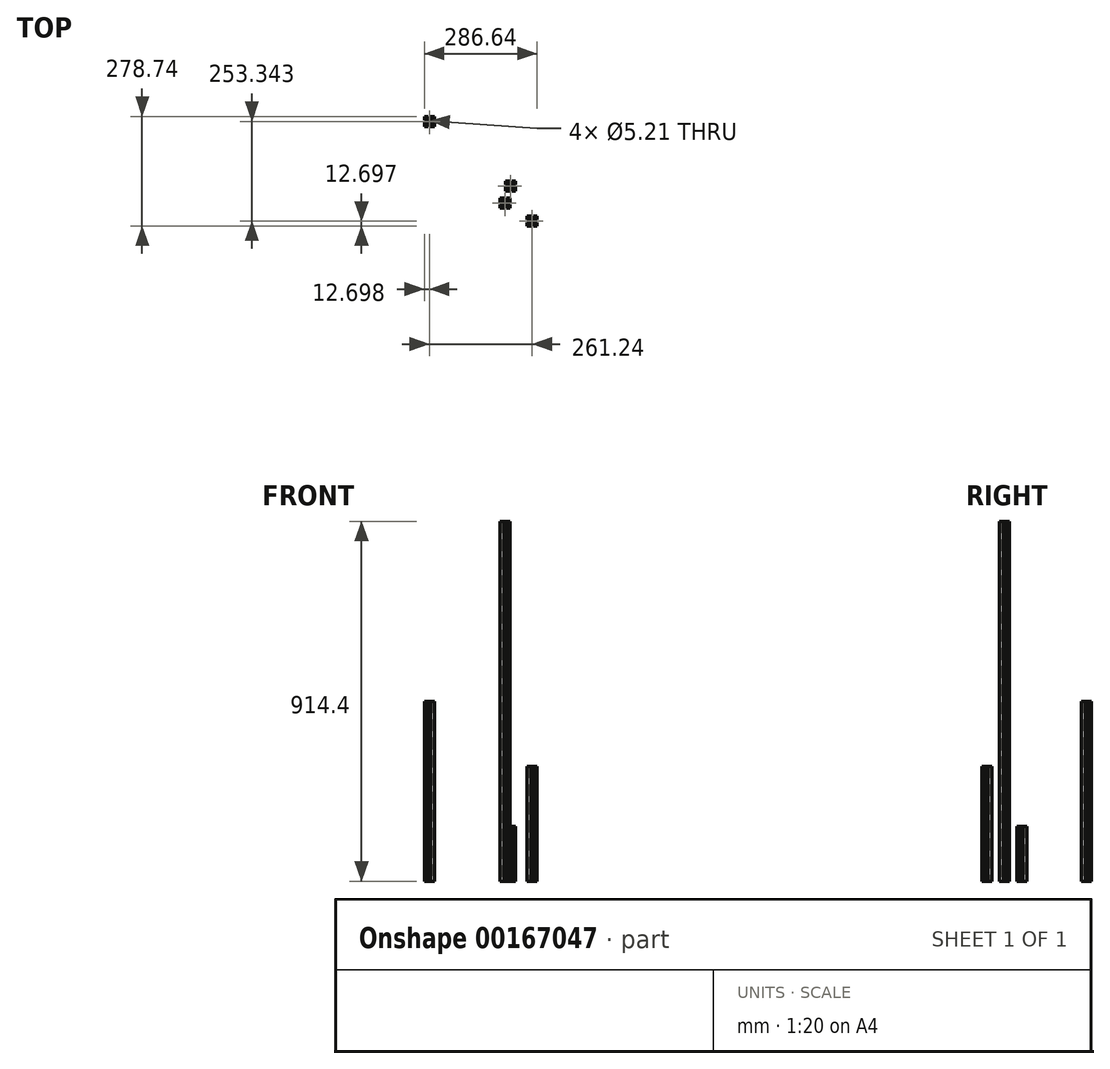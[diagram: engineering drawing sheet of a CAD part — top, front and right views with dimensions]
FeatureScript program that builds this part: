
annotation { "Feature Type Name" : "Feature", "Feature Type Description" : "" }
export const myFeature = defineFeature(function(context is Context, id is Id, definition is map)
    precondition{}
    {
        {
            var Q0;
            Q0=qCreatedBy(makeId("Top.planeOp"),FACE);
            var sketch = newSketch(context, id + "F0", { "sketchPlane" : qUnion([Q0])});
            skCircle(sketch, "E0", {"center": v(0, 0) * mm, "radius": 2.6 * mm});
            skLineSegment(sketch, "E1.bottom", {"start": v(-4.5, 4.5) * mm, "end": v(4.5, 4.5) * mm, "construction": true});
            skLineSegment(sketch, "E1.top", {"start": v(-4.5, -4.5) * mm, "end": v(4.5, -4.5) * mm, "construction": true});
            skLineSegment(sketch, "E1.left", {"start": v(-4.5, 4.5) * mm, "end": v(-4.5, -4.5) * mm, "construction": true});
            skLineSegment(sketch, "E1.right", {"start": v(4.5, 4.5) * mm, "end": v(4.5, -4.5) * mm, "construction": true});
            skPoint(sketch, "E2", {"position": v(-4.5, 0) * mm});
            skPoint(sketch, "E3", {"position": v(0, 4.5) * mm});
            skLineSegment(sketch, "E4", {"start": v(-2.54, 4.5) * mm, "end": v(2.54, 4.5) * mm});
            skLineSegment(sketch, "E5", {"start": v(2.54, 4.5) * mm, "end": v(8.2, 10.16) * mm});
            skLineSegment(sketch, "E6", {"start": v(8.2, 10.16) * mm, "end": v(3.24, 10.16) * mm});
            skLineSegment(sketch, "E7", {"start": v(3.24, 10.16) * mm, "end": v(3.24, 12.7) * mm});
            skLineSegment(sketch, "E8", {"start": v(3.24, 12.7) * mm, "end": v(12.7, 12.7) * mm});
            skLineSegment(sketch, "E9", {"start": v(12.7, 12.7) * mm, "end": v(12.7, 3.24) * mm});
            skLineSegment(sketch, "E10", {"start": v(12.7, 3.24) * mm, "end": v(10.16, 3.24) * mm});
            skLineSegment(sketch, "E11", {"start": v(10.16, 3.24) * mm, "end": v(10.16, 8.2) * mm});
            skLineSegment(sketch, "E12", {"start": v(10.16, 8.2) * mm, "end": v(4.5, 2.54) * mm});
            skLineSegment(sketch, "E13", {"start": v(4.5, 2.54) * mm, "end": v(4.5, -2.54) * mm});
            skLineSegment(sketch, "E14", {"start": v(4.5, -2.54) * mm, "end": v(10.16, -8.2) * mm});
            skLineSegment(sketch, "E15", {"start": v(10.16, -8.2) * mm, "end": v(10.16, -3.24) * mm});
            skLineSegment(sketch, "E16", {"start": v(10.16, -3.24) * mm, "end": v(12.7, -3.24) * mm});
            skLineSegment(sketch, "E17", {"start": v(12.7, -3.24) * mm, "end": v(12.7, -12.7) * mm});
            skLineSegment(sketch, "E18", {"start": v(12.7, -12.7) * mm, "end": v(3.24, -12.7) * mm});
            skLineSegment(sketch, "E19", {"start": v(3.24, -12.7) * mm, "end": v(3.24, -10.16) * mm});
            skLineSegment(sketch, "E20", {"start": v(3.24, -10.16) * mm, "end": v(8.2, -10.16) * mm});
            skLineSegment(sketch, "E21", {"start": v(8.2, -10.16) * mm, "end": v(2.54, -4.5) * mm});
            skLineSegment(sketch, "E22", {"start": v(2.54, -4.5) * mm, "end": v(-2.54, -4.5) * mm});
            skLineSegment(sketch, "E23", {"start": v(-2.54, -4.5) * mm, "end": v(-8.2, -10.16) * mm});
            skLineSegment(sketch, "E24", {"start": v(-8.2, -10.16) * mm, "end": v(-3.24, -10.16) * mm});
            skLineSegment(sketch, "E25", {"start": v(-3.24, -10.16) * mm, "end": v(-3.24, -12.7) * mm});
            skLineSegment(sketch, "E26", {"start": v(-3.24, -12.7) * mm, "end": v(-12.7, -12.7) * mm});
            skLineSegment(sketch, "E27", {"start": v(-12.7, -12.7) * mm, "end": v(-12.7, -3.24) * mm});
            skLineSegment(sketch, "E28", {"start": v(-12.7, -3.24) * mm, "end": v(-10.16, -3.24) * mm});
            skLineSegment(sketch, "E29", {"start": v(-10.16, -3.24) * mm, "end": v(-10.16, -8.2) * mm});
            skLineSegment(sketch, "E30", {"start": v(-10.16, -8.2) * mm, "end": v(-4.5, -2.54) * mm});
            skLineSegment(sketch, "E31", {"start": v(-4.5, -2.54) * mm, "end": v(-4.5, 2.54) * mm});
            skLineSegment(sketch, "E32", {"start": v(-4.5, 2.54) * mm, "end": v(-10.16, 8.2) * mm});
            skLineSegment(sketch, "E33", {"start": v(-10.16, 8.2) * mm, "end": v(-10.16, 3.24) * mm});
            skLineSegment(sketch, "E34", {"start": v(-10.16, 3.24) * mm, "end": v(-12.7, 3.24) * mm});
            skLineSegment(sketch, "E35", {"start": v(-12.7, 3.24) * mm, "end": v(-12.7, 12.7) * mm});
            skLineSegment(sketch, "E36", {"start": v(-12.7, 12.7) * mm, "end": v(-3.24, 12.7) * mm});
            skLineSegment(sketch, "E37", {"start": v(-3.24, 12.7) * mm, "end": v(-3.24, 10.16) * mm});
            skLineSegment(sketch, "E38", {"start": v(-3.24, 10.16) * mm, "end": v(-8.2, 10.16) * mm});
            skLineSegment(sketch, "E39", {"start": v(-8.2, 10.16) * mm, "end": v(-2.54, 4.5) * mm});
            skLineSegment(sketch, "E40", {"start": v(-3.24, 12.7) * mm, "end": v(3.24, 12.7) * mm, "construction": true});
            skLineSegment(sketch, "E41", {"start": v(12.7, 3.24) * mm, "end": v(12.7, -3.24) * mm, "construction": true});
            skLineSegment(sketch, "E42", {"start": v(3.24, -12.7) * mm, "end": v(-3.24, -12.7) * mm, "construction": true});
            skLineSegment(sketch, "E43", {"start": v(-12.7, -3.24) * mm, "end": v(-12.7, 3.24) * mm, "construction": true});
            skPoint(sketch, "E44", {"position": v(-12.7, 0) * mm});
            skPoint(sketch, "E45", {"position": v(0, 12.7) * mm});
            skPoint(sketch, "E46", {"position": v(12.7, 0) * mm});
            skPoint(sketch, "E47", {"position": v(0, -12.7) * mm});
            skSolve(sketch);
        }
        {
            var Q0;
            Q0 = qSketchRegion(id + "F0", true);
            extrude(context, id + "F1", {"entities" : qUnion([Q0]), "depth" : 914.4 * mm});
        }
        {
            var Q0;
            Q0=qCreatedBy(makeId("Top.planeOp"),FACE);
            var sketch = newSketch(context, id + "F2", { "sketchPlane" : qUnion([Q0])});
            skCircle(sketch, "E48", {"center": v(68.7, -45.38) * mm, "radius": 2.6 * mm});
            skLineSegment(sketch, "E49.bottom", {"start": v(64.19, -40.87) * mm, "end": v(73.2, -40.87) * mm, "construction": true});
            skLineSegment(sketch, "E49.top", {"start": v(64.19, -49.9) * mm, "end": v(73.2, -49.9) * mm, "construction": true});
            skLineSegment(sketch, "E49.left", {"start": v(64.19, -40.87) * mm, "end": v(64.19, -49.9) * mm, "construction": true});
            skLineSegment(sketch, "E49.right", {"start": v(73.2, -40.87) * mm, "end": v(73.2, -49.9) * mm, "construction": true});
            skPoint(sketch, "E50", {"position": v(64.19, -45.38) * mm});
            skPoint(sketch, "E51", {"position": v(68.7, -40.87) * mm});
            skLineSegment(sketch, "E52", {"start": v(66.16, -40.87) * mm, "end": v(71.24, -40.87) * mm});
            skLineSegment(sketch, "E53", {"start": v(71.24, -40.87) * mm, "end": v(76.89, -35.22) * mm});
            skLineSegment(sketch, "E54", {"start": v(76.89, -35.22) * mm, "end": v(71.94, -35.22) * mm});
            skLineSegment(sketch, "E55", {"start": v(71.94, -35.22) * mm, "end": v(71.94, -32.68) * mm});
            skLineSegment(sketch, "E56", {"start": v(71.94, -32.68) * mm, "end": v(81.4, -32.68) * mm});
            skLineSegment(sketch, "E57", {"start": v(81.4, -32.68) * mm, "end": v(81.4, -42.14) * mm});
            skLineSegment(sketch, "E58", {"start": v(81.4, -42.14) * mm, "end": v(78.86, -42.14) * mm});
            skLineSegment(sketch, "E59", {"start": v(78.86, -42.14) * mm, "end": v(78.86, -37.2) * mm});
            skLineSegment(sketch, "E60", {"start": v(78.86, -37.2) * mm, "end": v(73.2, -42.84) * mm});
            skLineSegment(sketch, "E61", {"start": v(73.2, -42.84) * mm, "end": v(73.2, -47.92) * mm});
            skLineSegment(sketch, "E62", {"start": v(73.2, -47.92) * mm, "end": v(78.86, -53.57) * mm});
            skLineSegment(sketch, "E63", {"start": v(78.86, -53.57) * mm, "end": v(78.86, -48.62) * mm});
            skLineSegment(sketch, "E64", {"start": v(78.86, -48.62) * mm, "end": v(81.4, -48.62) * mm});
            skLineSegment(sketch, "E65", {"start": v(81.4, -48.62) * mm, "end": v(81.4, -58.08) * mm});
            skLineSegment(sketch, "E66", {"start": v(81.4, -58.08) * mm, "end": v(71.94, -58.08) * mm});
            skLineSegment(sketch, "E67", {"start": v(71.94, -58.08) * mm, "end": v(71.94, -55.54) * mm});
            skLineSegment(sketch, "E68", {"start": v(71.94, -55.54) * mm, "end": v(76.89, -55.54) * mm});
            skLineSegment(sketch, "E69", {"start": v(76.89, -55.54) * mm, "end": v(71.24, -49.9) * mm});
            skLineSegment(sketch, "E70", {"start": v(71.24, -49.9) * mm, "end": v(66.16, -49.9) * mm});
            skLineSegment(sketch, "E71", {"start": v(66.16, -49.9) * mm, "end": v(60.5, -55.54) * mm});
            skLineSegment(sketch, "E72", {"start": v(60.5, -55.54) * mm, "end": v(65.46, -55.54) * mm});
            skLineSegment(sketch, "E73", {"start": v(65.46, -55.54) * mm, "end": v(65.46, -58.08) * mm});
            skLineSegment(sketch, "E74", {"start": v(65.46, -58.08) * mm, "end": v(56, -58.08) * mm});
            skLineSegment(sketch, "E75", {"start": v(56, -58.08) * mm, "end": v(56, -48.62) * mm});
            skLineSegment(sketch, "E76", {"start": v(56, -48.62) * mm, "end": v(58.54, -48.62) * mm});
            skLineSegment(sketch, "E77", {"start": v(58.54, -48.62) * mm, "end": v(58.54, -53.57) * mm});
            skLineSegment(sketch, "E78", {"start": v(58.54, -53.57) * mm, "end": v(64.19, -47.92) * mm});
            skLineSegment(sketch, "E79", {"start": v(64.19, -47.92) * mm, "end": v(64.19, -42.84) * mm});
            skLineSegment(sketch, "E80", {"start": v(64.19, -42.84) * mm, "end": v(58.54, -37.2) * mm});
            skLineSegment(sketch, "E81", {"start": v(58.54, -37.2) * mm, "end": v(58.54, -42.14) * mm});
            skLineSegment(sketch, "E82", {"start": v(58.54, -42.14) * mm, "end": v(56, -42.14) * mm});
            skLineSegment(sketch, "E83", {"start": v(56, -42.14) * mm, "end": v(56, -32.68) * mm});
            skLineSegment(sketch, "E84", {"start": v(56, -32.68) * mm, "end": v(65.46, -32.68) * mm});
            skLineSegment(sketch, "E85", {"start": v(65.46, -32.68) * mm, "end": v(65.46, -35.22) * mm});
            skLineSegment(sketch, "E86", {"start": v(65.46, -35.22) * mm, "end": v(60.5, -35.22) * mm});
            skLineSegment(sketch, "E87", {"start": v(60.5, -35.22) * mm, "end": v(66.16, -40.87) * mm});
            skLineSegment(sketch, "E88", {"start": v(65.46, -32.68) * mm, "end": v(71.94, -32.68) * mm, "construction": true});
            skLineSegment(sketch, "E89", {"start": v(81.4, -42.14) * mm, "end": v(81.4, -48.62) * mm, "construction": true});
            skLineSegment(sketch, "E90", {"start": v(71.94, -58.08) * mm, "end": v(65.46, -58.08) * mm, "construction": true});
            skLineSegment(sketch, "E91", {"start": v(56, -48.62) * mm, "end": v(56, -42.14) * mm, "construction": true});
            skPoint(sketch, "E92", {"position": v(56, -45.38) * mm});
            skPoint(sketch, "E93", {"position": v(68.7, -32.68) * mm});
            skPoint(sketch, "E94", {"position": v(81.4, -45.38) * mm});
            skPoint(sketch, "E95", {"position": v(68.7, -58.08) * mm});
            skSolve(sketch);
        }
        {
            var Q0;
            Q0 = qSketchRegion(id + "F2", true);
            extrude(context, id + "F3", {"entities" : qUnion([Q0]), "depth" : 292.1 * mm});
        }
        {
            var Q0;
            Q0=qCreatedBy(makeId("Top.planeOp"),FACE);
            var sketch = newSketch(context, id + "F4", { "sketchPlane" : qUnion([Q0])});
            skCircle(sketch, "E96", {"center": v(14.18, 43.76) * mm, "radius": 2.6 * mm});
            skLineSegment(sketch, "E97.bottom", {"start": v(9.67, 48.27) * mm, "end": v(18.69, 48.27) * mm, "construction": true});
            skLineSegment(sketch, "E97.top", {"start": v(9.67, 39.25) * mm, "end": v(18.69, 39.25) * mm, "construction": true});
            skLineSegment(sketch, "E97.left", {"start": v(9.67, 48.27) * mm, "end": v(9.67, 39.25) * mm, "construction": true});
            skLineSegment(sketch, "E97.right", {"start": v(18.69, 48.27) * mm, "end": v(18.69, 39.25) * mm, "construction": true});
            skPoint(sketch, "E98", {"position": v(9.67, 43.76) * mm});
            skPoint(sketch, "E99", {"position": v(14.18, 48.27) * mm});
            skLineSegment(sketch, "E100", {"start": v(11.64, 48.27) * mm, "end": v(16.72, 48.27) * mm});
            skLineSegment(sketch, "E101", {"start": v(16.72, 48.27) * mm, "end": v(22.37, 53.92) * mm});
            skLineSegment(sketch, "E102", {"start": v(22.37, 53.92) * mm, "end": v(17.42, 53.92) * mm});
            skLineSegment(sketch, "E103", {"start": v(17.42, 53.92) * mm, "end": v(17.42, 56.46) * mm});
            skLineSegment(sketch, "E104", {"start": v(17.42, 56.46) * mm, "end": v(26.88, 56.46) * mm});
            skLineSegment(sketch, "E105", {"start": v(26.88, 56.46) * mm, "end": v(26.88, 47) * mm});
            skLineSegment(sketch, "E106", {"start": v(26.88, 47) * mm, "end": v(24.34, 47) * mm});
            skLineSegment(sketch, "E107", {"start": v(24.34, 47) * mm, "end": v(24.34, 51.95) * mm});
            skLineSegment(sketch, "E108", {"start": v(24.34, 51.95) * mm, "end": v(18.69, 46.3) * mm});
            skLineSegment(sketch, "E109", {"start": v(18.69, 46.3) * mm, "end": v(18.69, 41.22) * mm});
            skLineSegment(sketch, "E110", {"start": v(18.69, 41.22) * mm, "end": v(24.34, 35.57) * mm});
            skLineSegment(sketch, "E111", {"start": v(24.34, 35.57) * mm, "end": v(24.34, 40.52) * mm});
            skLineSegment(sketch, "E112", {"start": v(24.34, 40.52) * mm, "end": v(26.88, 40.52) * mm});
            skLineSegment(sketch, "E113", {"start": v(26.88, 40.52) * mm, "end": v(26.88, 31.06) * mm});
            skLineSegment(sketch, "E114", {"start": v(26.88, 31.06) * mm, "end": v(17.42, 31.06) * mm});
            skLineSegment(sketch, "E115", {"start": v(17.42, 31.06) * mm, "end": v(17.42, 33.6) * mm});
            skLineSegment(sketch, "E116", {"start": v(17.42, 33.6) * mm, "end": v(22.37, 33.6) * mm});
            skLineSegment(sketch, "E117", {"start": v(22.37, 33.6) * mm, "end": v(16.72, 39.25) * mm});
            skLineSegment(sketch, "E118", {"start": v(16.72, 39.25) * mm, "end": v(11.64, 39.25) * mm});
            skLineSegment(sketch, "E119", {"start": v(11.64, 39.25) * mm, "end": v(5.99, 33.6) * mm});
            skLineSegment(sketch, "E120", {"start": v(5.99, 33.6) * mm, "end": v(10.94, 33.6) * mm});
            skLineSegment(sketch, "E121", {"start": v(10.94, 33.6) * mm, "end": v(10.94, 31.06) * mm});
            skLineSegment(sketch, "E122", {"start": v(10.94, 31.06) * mm, "end": v(1.48, 31.06) * mm});
            skLineSegment(sketch, "E123", {"start": v(1.48, 31.06) * mm, "end": v(1.48, 40.52) * mm});
            skLineSegment(sketch, "E124", {"start": v(1.48, 40.52) * mm, "end": v(4.02, 40.52) * mm});
            skLineSegment(sketch, "E125", {"start": v(4.02, 40.52) * mm, "end": v(4.02, 35.57) * mm});
            skLineSegment(sketch, "E126", {"start": v(4.02, 35.57) * mm, "end": v(9.67, 41.22) * mm});
            skLineSegment(sketch, "E127", {"start": v(9.67, 41.22) * mm, "end": v(9.67, 46.3) * mm});
            skLineSegment(sketch, "E128", {"start": v(9.67, 46.3) * mm, "end": v(4.02, 51.95) * mm});
            skLineSegment(sketch, "E129", {"start": v(4.02, 51.95) * mm, "end": v(4.02, 47) * mm});
            skLineSegment(sketch, "E130", {"start": v(4.02, 47) * mm, "end": v(1.48, 47) * mm});
            skLineSegment(sketch, "E131", {"start": v(1.48, 47) * mm, "end": v(1.48, 56.46) * mm});
            skLineSegment(sketch, "E132", {"start": v(1.48, 56.46) * mm, "end": v(10.94, 56.46) * mm});
            skLineSegment(sketch, "E133", {"start": v(10.94, 56.46) * mm, "end": v(10.94, 53.92) * mm});
            skLineSegment(sketch, "E134", {"start": v(10.94, 53.92) * mm, "end": v(5.99, 53.92) * mm});
            skLineSegment(sketch, "E135", {"start": v(5.99, 53.92) * mm, "end": v(11.64, 48.27) * mm});
            skLineSegment(sketch, "E136", {"start": v(10.94, 56.46) * mm, "end": v(17.42, 56.46) * mm, "construction": true});
            skLineSegment(sketch, "E137", {"start": v(26.88, 47) * mm, "end": v(26.88, 40.52) * mm, "construction": true});
            skLineSegment(sketch, "E138", {"start": v(17.42, 31.06) * mm, "end": v(10.94, 31.06) * mm, "construction": true});
            skLineSegment(sketch, "E139", {"start": v(1.48, 40.52) * mm, "end": v(1.48, 47) * mm, "construction": true});
            skPoint(sketch, "E140", {"position": v(1.48, 43.76) * mm});
            skPoint(sketch, "E141", {"position": v(14.18, 56.46) * mm});
            skPoint(sketch, "E142", {"position": v(26.88, 43.76) * mm});
            skPoint(sketch, "E143", {"position": v(14.18, 31.06) * mm});
            skSolve(sketch);
        }
        {
            var Q0;
            Q0 = qSketchRegion(id + "F4", true);
            extrude(context, id + "F5", {"entities" : qUnion([Q0]), "depth" : 139.7 * mm});
        }
        {
            var Q0;
            Q0=qCreatedBy(makeId("Top.planeOp"),FACE);
            var sketch = newSketch(context, id + "F6", { "sketchPlane" : qUnion([Q0])});
            skCircle(sketch, "E144", {"center": v(-192.54, 207.96) * mm, "radius": 2.6 * mm});
            skLineSegment(sketch, "E145.bottom", {"start": v(-197.05, 212.47) * mm, "end": v(-188.03, 212.47) * mm, "construction": true});
            skLineSegment(sketch, "E145.top", {"start": v(-197.05, 203.45) * mm, "end": v(-188.03, 203.45) * mm, "construction": true});
            skLineSegment(sketch, "E145.left", {"start": v(-197.05, 212.47) * mm, "end": v(-197.05, 203.45) * mm, "construction": true});
            skLineSegment(sketch, "E145.right", {"start": v(-188.03, 212.47) * mm, "end": v(-188.03, 203.45) * mm, "construction": true});
            skPoint(sketch, "E146", {"position": v(-197.05, 207.96) * mm});
            skPoint(sketch, "E147", {"position": v(-192.54, 212.47) * mm});
            skLineSegment(sketch, "E148", {"start": v(-195.08, 212.47) * mm, "end": v(-190, 212.47) * mm});
            skLineSegment(sketch, "E149", {"start": v(-190, 212.47) * mm, "end": v(-184.35, 218.12) * mm});
            skLineSegment(sketch, "E150", {"start": v(-184.35, 218.12) * mm, "end": v(-189.3, 218.12) * mm});
            skLineSegment(sketch, "E151", {"start": v(-189.3, 218.12) * mm, "end": v(-189.3, 220.66) * mm});
            skLineSegment(sketch, "E152", {"start": v(-189.3, 220.66) * mm, "end": v(-179.84, 220.66) * mm});
            skLineSegment(sketch, "E153", {"start": v(-179.84, 220.66) * mm, "end": v(-179.84, 211.2) * mm});
            skLineSegment(sketch, "E154", {"start": v(-179.84, 211.2) * mm, "end": v(-182.38, 211.2) * mm});
            skLineSegment(sketch, "E155", {"start": v(-182.38, 211.2) * mm, "end": v(-182.38, 216.15) * mm});
            skLineSegment(sketch, "E156", {"start": v(-182.38, 216.15) * mm, "end": v(-188.03, 210.5) * mm});
            skLineSegment(sketch, "E157", {"start": v(-188.03, 210.5) * mm, "end": v(-188.03, 205.42) * mm});
            skLineSegment(sketch, "E158", {"start": v(-188.03, 205.42) * mm, "end": v(-182.38, 199.77) * mm});
            skLineSegment(sketch, "E159", {"start": v(-182.38, 199.77) * mm, "end": v(-182.38, 204.72) * mm});
            skLineSegment(sketch, "E160", {"start": v(-182.38, 204.72) * mm, "end": v(-179.84, 204.72) * mm});
            skLineSegment(sketch, "E161", {"start": v(-179.84, 204.72) * mm, "end": v(-179.84, 195.26) * mm});
            skLineSegment(sketch, "E162", {"start": v(-179.84, 195.26) * mm, "end": v(-189.3, 195.26) * mm});
            skLineSegment(sketch, "E163", {"start": v(-189.3, 195.26) * mm, "end": v(-189.3, 197.8) * mm});
            skLineSegment(sketch, "E164", {"start": v(-189.3, 197.8) * mm, "end": v(-184.35, 197.8) * mm});
            skLineSegment(sketch, "E165", {"start": v(-184.35, 197.8) * mm, "end": v(-190, 203.45) * mm});
            skLineSegment(sketch, "E166", {"start": v(-190, 203.45) * mm, "end": v(-195.08, 203.45) * mm});
            skLineSegment(sketch, "E167", {"start": v(-195.08, 203.45) * mm, "end": v(-200.73, 197.8) * mm});
            skLineSegment(sketch, "E168", {"start": v(-200.73, 197.8) * mm, "end": v(-195.78, 197.8) * mm});
            skLineSegment(sketch, "E169", {"start": v(-195.78, 197.8) * mm, "end": v(-195.78, 195.26) * mm});
            skLineSegment(sketch, "E170", {"start": v(-195.78, 195.26) * mm, "end": v(-205.24, 195.26) * mm});
            skLineSegment(sketch, "E171", {"start": v(-205.24, 195.26) * mm, "end": v(-205.24, 204.72) * mm});
            skLineSegment(sketch, "E172", {"start": v(-205.24, 204.72) * mm, "end": v(-202.7, 204.72) * mm});
            skLineSegment(sketch, "E173", {"start": v(-202.7, 204.72) * mm, "end": v(-202.7, 199.77) * mm});
            skLineSegment(sketch, "E174", {"start": v(-202.7, 199.77) * mm, "end": v(-197.05, 205.42) * mm});
            skLineSegment(sketch, "E175", {"start": v(-197.05, 205.42) * mm, "end": v(-197.05, 210.5) * mm});
            skLineSegment(sketch, "E176", {"start": v(-197.05, 210.5) * mm, "end": v(-202.7, 216.15) * mm});
            skLineSegment(sketch, "E177", {"start": v(-202.7, 216.15) * mm, "end": v(-202.7, 211.2) * mm});
            skLineSegment(sketch, "E178", {"start": v(-202.7, 211.2) * mm, "end": v(-205.24, 211.2) * mm});
            skLineSegment(sketch, "E179", {"start": v(-205.24, 211.2) * mm, "end": v(-205.24, 220.66) * mm});
            skLineSegment(sketch, "E180", {"start": v(-205.24, 220.66) * mm, "end": v(-195.78, 220.66) * mm});
            skLineSegment(sketch, "E181", {"start": v(-195.78, 220.66) * mm, "end": v(-195.78, 218.12) * mm});
            skLineSegment(sketch, "E182", {"start": v(-195.78, 218.12) * mm, "end": v(-200.73, 218.12) * mm});
            skLineSegment(sketch, "E183", {"start": v(-200.73, 218.12) * mm, "end": v(-195.08, 212.47) * mm});
            skLineSegment(sketch, "E184", {"start": v(-195.78, 220.66) * mm, "end": v(-189.3, 220.66) * mm, "construction": true});
            skLineSegment(sketch, "E185", {"start": v(-179.84, 211.2) * mm, "end": v(-179.84, 204.72) * mm, "construction": true});
            skLineSegment(sketch, "E186", {"start": v(-189.3, 195.26) * mm, "end": v(-195.78, 195.26) * mm, "construction": true});
            skLineSegment(sketch, "E187", {"start": v(-205.24, 204.72) * mm, "end": v(-205.24, 211.2) * mm, "construction": true});
            skPoint(sketch, "E188", {"position": v(-205.24, 207.96) * mm});
            skPoint(sketch, "E189", {"position": v(-192.54, 220.66) * mm});
            skPoint(sketch, "E190", {"position": v(-179.84, 207.96) * mm});
            skPoint(sketch, "E191", {"position": v(-192.54, 195.26) * mm});
            skSolve(sketch);
        }
        {
            var Q0;
            Q0 = qSketchRegion(id + "F6", true);
            extrude(context, id + "F7", {"entities" : qUnion([Q0]), "depth" : 457.2 * mm});
        }
    });
